# Revit family: P200921MX-047c_MGR8800FZ
name_source: partatom
category: Specialty Equipment
units: mm (PartAtom-declared; Revit-internal decimal feet)

## family parameters
Always vertical = Yes
Cut with Voids When Loaded = No
Enable Cutting in Views = No
Maintain Annotation Orientation = No
Part Type = Normal
Room Calculation Point = No
Round Connector Dimension = Use Diameter
Shared = No
Work Plane-Based = No

## types (1)
- MGR8800FZ
    Amps = 0 A
    Body Material = ARCAT - Metal - Steel - Black
    Clearance Material = ARCAT - Clearance
    Connector Material = ARCAT - Metal - Aluminum
    Cooking Grate Material = ARCAT - Metal - Cast Iron 1/4" Plate
    Default Elevation = 0"
    Depth = 27 7/8"
    Description = 30-Inch Wide Gas Range With True Convection And Power Preheat - 5.8 Cu. Ft.
Cuisinière au gaz avec convection véritable et préchauffage rapide, 30 po, 5.8 pi3
    Dimension Guide = http://whirlpool.com
http://whirlpool.com
    Display Panel Material = ARCAT - Glass - Black
    Door Material = ARCAT - Metal - Steel - Stainless
    Family Name = Cooking
    Feature 1 = Fingerprint Resistant Stainless Steel
Acier inoxydable résistant aux traces de doigts
    Feature 2 = Power Preheat
Préchauffage rapide
    Feature 3 = Power™ Burner
Brûleur Power™
    Glass Material = ARCAT - Glass - Tempered - Black
    Handle Material = ARCAT - Metal - Steel -Gray - Light
    Height = 47 7/8"
    Installation-Fabrication = https://www.whirlpool.com
http://access.whirlpool.com Instruction&sku=MGR8800FZ&language=FR
    Knob Material = ARCAT - Metal - Steel -Gray - Light
    Leg Material = ARCAT - Plastic - Black
    Manufacturer = Maytag
    Model = MGR8800FZ
    Voltage = 0 V
    Width = 29 7/8"

## geometry (parser evidence)
native form markers: Sweep x3
no freeform markers — native parametric forms only
